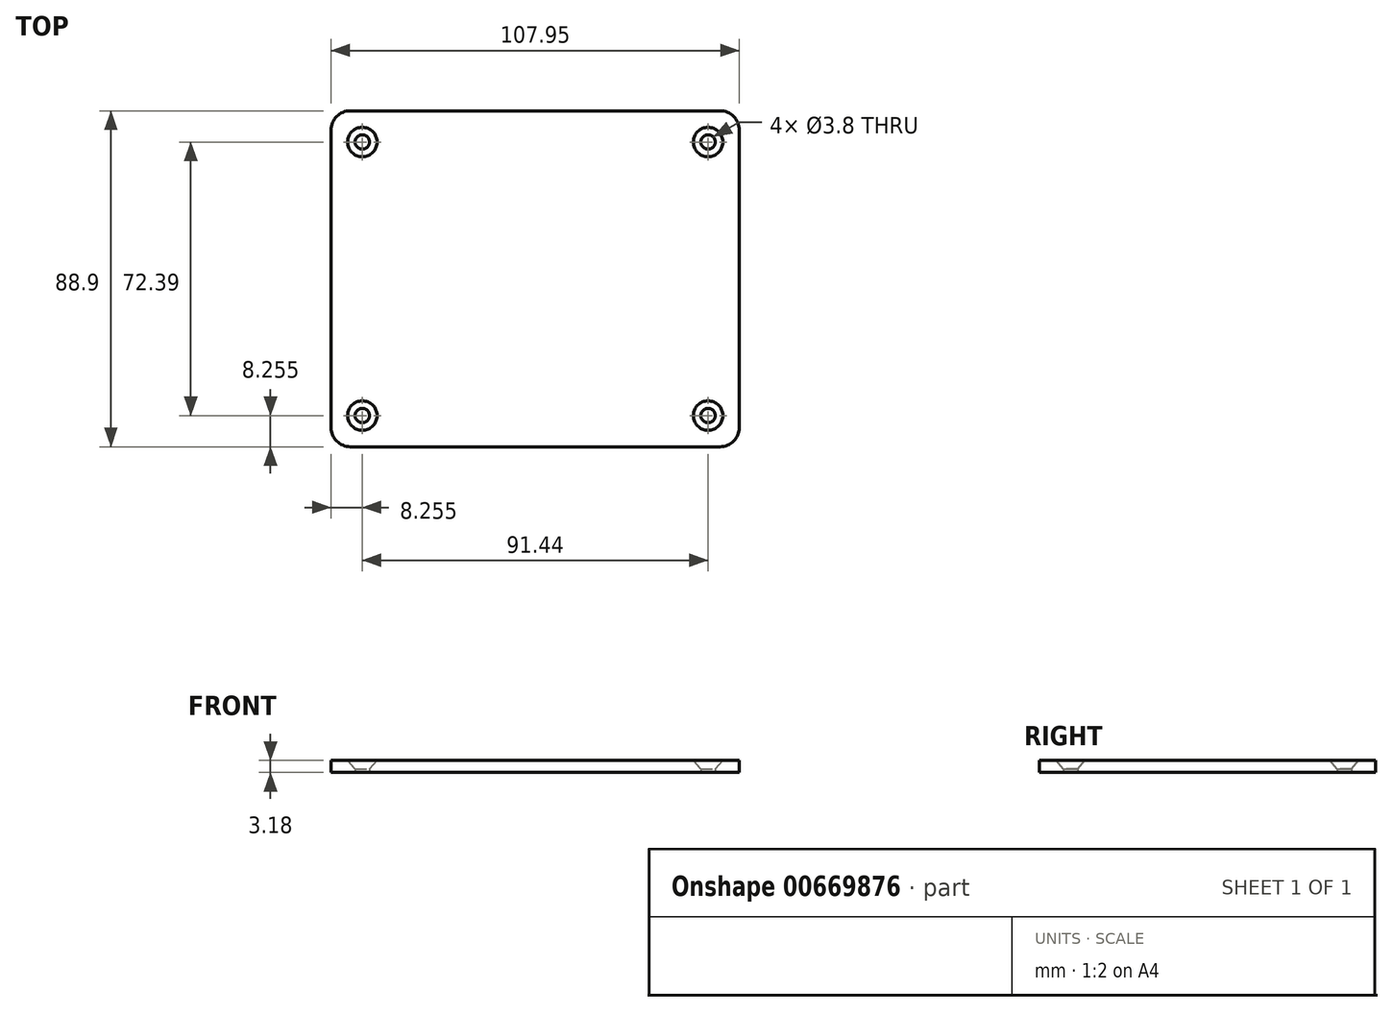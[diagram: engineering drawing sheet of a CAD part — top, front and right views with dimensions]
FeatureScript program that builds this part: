
annotation { "Feature Type Name" : "Feature", "Feature Type Description" : "" }
export const myFeature = defineFeature(function(context is Context, id is Id, definition is map)
    precondition{}
    {
        {
            var Q0;
            Q0=qCreatedBy(makeId("Top.planeOp"),FACE);
            var sketch = newSketch(context, id + "F0", { "sketchPlane" : qUnion([Q0])});
            skLineSegment(sketch, "E0.bottom", {"start": v(0, 0) * mm, "end": v(107.95, 0) * mm});
            skLineSegment(sketch, "E0.top", {"start": v(0, 88.9) * mm, "end": v(107.95, 88.9) * mm});
            skLineSegment(sketch, "E0.left", {"start": v(0, 0) * mm, "end": v(0, 88.9) * mm});
            skLineSegment(sketch, "E0.right", {"start": v(107.95, 0) * mm, "end": v(107.95, 88.9) * mm});
            skSolve(sketch);
        }
        {
            var Q0;
            Q0=qSketchRegion(id+"F0",true);
            extrude(context, id + "F1", {"entities" : qUnion([Q0]), "depth" : 3.17 * mm});
        }
        {
            var Q0;
            Q0=makeQuery(id+"F1.opExtrude","CAP_FACE",FACE,{"disambiguationData":[OSD([sQuery(id+"F0.wireOp",EDGE,"E0.bottom"),sQuery(id+"F0.wireOp",EDGE,"E0.top"),sQuery(id+"F0.wireOp",EDGE,"E0.left"),sQuery(id+"F0.wireOp",EDGE,"E0.right")])],"isStart":false});
            var sketch = newSketch(context, id + "F2", { "sketchPlane" : qUnion([Q0])});
            skLineSegment(sketch, "E1", {"start": v(53.97, 88.9) * mm, "end": v(53.98, 0) * mm, "construction": true});
            skLineSegment(sketch, "E2", {"start": v(0, 44.45) * mm, "end": v(107.95, 44.45) * mm, "construction": true});
            skPoint(sketch, "E3", {"position": v(8.25, 80.65) * mm});
            skPoint(sketch, "E4", {"position": v(99.7, 80.65) * mm});
            skPoint(sketch, "E5", {"position": v(99.7, 8.26) * mm});
            skPoint(sketch, "E6", {"position": v(8.26, 8.26) * mm});
            skSolve(sketch);
        }
        {
            var Q0;
            Q0=sQuery(id+"F2.wireOp",VERTEX,"E3");
            var Q1;
            Q1=sQuery(id+"F2.wireOp",VERTEX,"E4");
            var Q2;
            Q2=sQuery(id+"F2.wireOp",VERTEX,"E5");
            var Q3;
            Q3=sQuery(id+"F2.wireOp",VERTEX,"E6");
            var Q4;
            Q4=makeQuery(id+"F1.opExtrude","SWEPT_BODY",BODY,{"disambiguationData":[OSD([sQuery(id+"F0.wireOp",EDGE,"E0.bottom"),sQuery(id+"F0.wireOp",EDGE,"E0.top"),sQuery(id+"F0.wireOp",EDGE,"E0.left"),sQuery(id+"F0.wireOp",EDGE,"E0.right")])]});
            hole(context, id + "F3", {"style" : HoleStyle.C_SINK, "endStyle" : HoleEndStyle.THROUGH, "standardTappedOrClearance" : lookupTablePath({ "standard" : "ANSI", "fit" : "Normal (ASME)", "size" : "#6", "type" : "Clearance" }), "standardBlindInLast" : lookupTablePath({ "fit" : "Free", "standard" : "ANSI", "size" : "#6", "type" : "Clearance" }), "holeDiameter" : 3.8 * mm, "cSinkDiameter" : 7.8 * mm, "cSinkAngle" : 82 * degree, "tappedDepth" : 2.77 * mm, "tapClearance" : 3, "startFromSketch" : true, "locations" : qUnion([Q0, Q1, Q2, Q3]), "scope" : qUnion([Q4])});
        }
        {
            var Q0;
            Q0=makeQuery(id+"F1.opExtrude","SWEPT_EDGE",EDGE,{"disambiguationData":[OSD([sQuery(id+"F0.wireOp",EDGE,"E0.bottom"),sQuery(id+"F0.wireOp",EDGE,"E0.left")])]});
            var Q1;
            Q1=makeQuery(id+"F1.opExtrude","SWEPT_EDGE",EDGE,{"disambiguationData":[OSD([sQuery(id+"F0.wireOp",EDGE,"E0.bottom"),sQuery(id+"F0.wireOp",EDGE,"E0.right")])]});
            var Q2;
            Q2=makeQuery(id+"F1.opExtrude","SWEPT_EDGE",EDGE,{"disambiguationData":[OSD([sQuery(id+"F0.wireOp",EDGE,"E0.top"),sQuery(id+"F0.wireOp",EDGE,"E0.right")])]});
            var Q3;
            Q3=makeQuery(id+"F1.opExtrude","SWEPT_EDGE",EDGE,{"disambiguationData":[OSD([sQuery(id+"F0.wireOp",EDGE,"E0.top"),sQuery(id+"F0.wireOp",EDGE,"E0.left")])]});
            fillet(context, id + "F4", {"entities" : qUnion([Q0, Q1, Q2, Q3]), "radius" : 5.08 * mm, "tangentPropagation" : true, "allowEdgeOverflow" : false});
        }
    });
